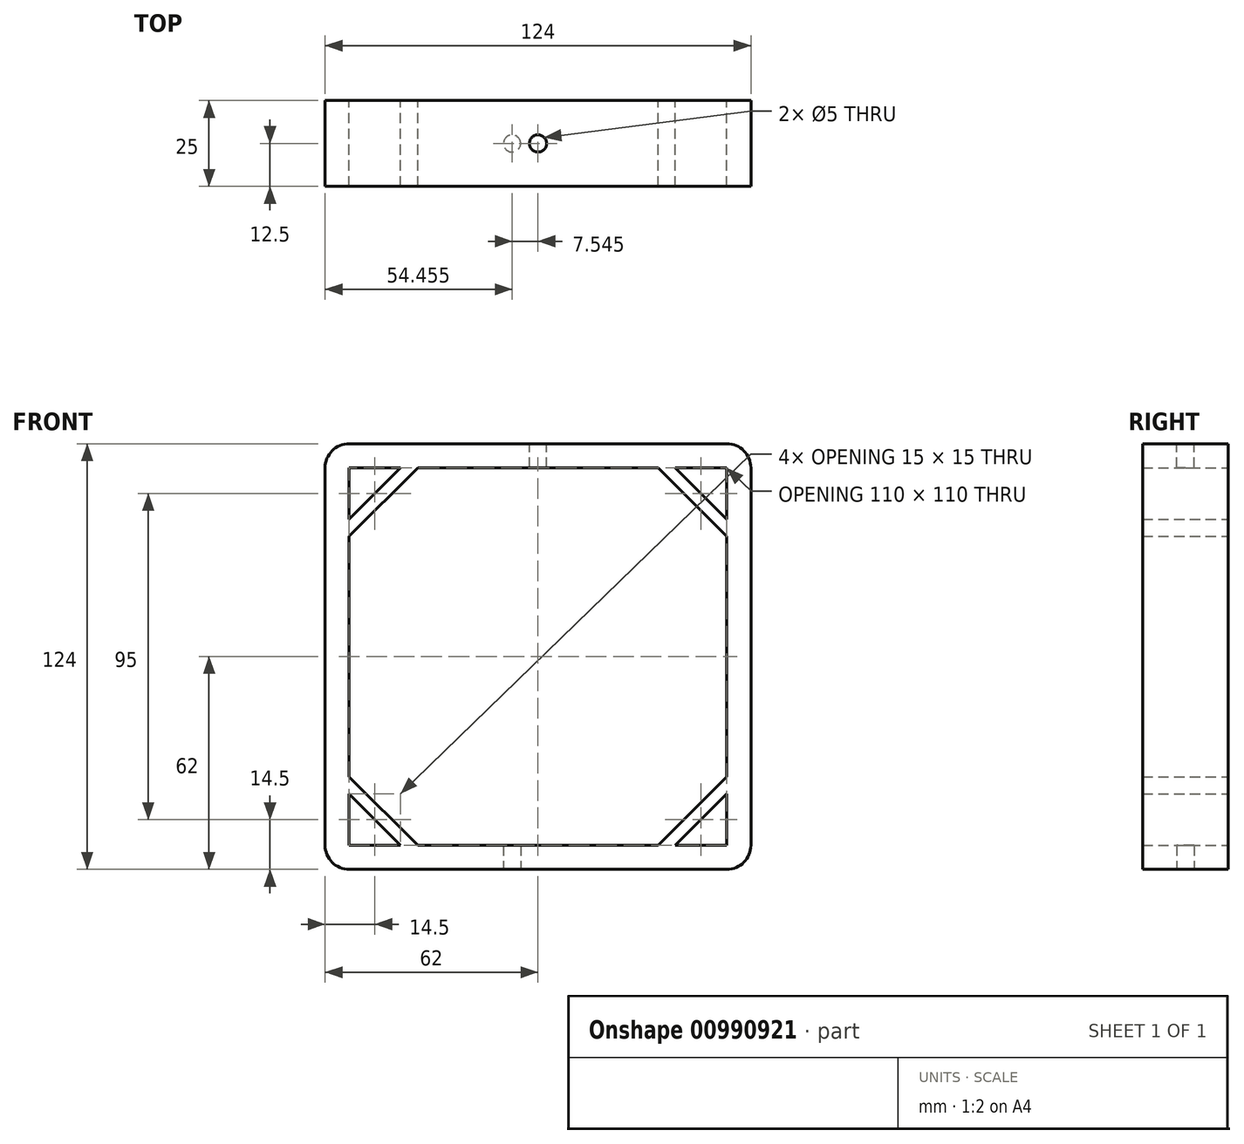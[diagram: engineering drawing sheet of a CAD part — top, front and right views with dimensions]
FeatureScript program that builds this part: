
annotation { "Feature Type Name" : "Feature", "Feature Type Description" : "" }
export const myFeature = defineFeature(function(context is Context, id is Id, definition is map)
    precondition{}
    {
        {
            var Q0;
            Q0=qCreatedBy(makeId("Front.planeOp"),FACE);
            var sketch = newSketch(context, id + "F0", { "sketchPlane" : qUnion([Q0])});
            skLineSegment(sketch, "E0.bottom", {"start": v(55, 55) * mm, "end": v(-55, 55) * mm});
            skLineSegment(sketch, "E0.top", {"start": v(55, 62) * mm, "end": v(-55, 62) * mm});
            skLineSegment(sketch, "E0.left", {"start": v(55, 55) * mm, "end": v(55, 62) * mm});
            skLineSegment(sketch, "E0.right", {"start": v(-55, 55) * mm, "end": v(-55, 62) * mm, "construction": true});
            skPoint(sketch, "E0.middle", {"position": v(0, 58.5) * mm});
            skLineSegment(sketch, "E1.MirrorCS", {"start": v(-55, -55) * mm, "end": v(-55, -62) * mm});
            skLineSegment(sketch, "E2.MirrorCS", {"start": v(55, -62) * mm, "end": v(-55, -62) * mm});
            skLineSegment(sketch, "E3.MirrorCS", {"start": v(55, -55) * mm, "end": v(55, -62) * mm, "construction": true});
            skLineSegment(sketch, "E4.MirrorCS", {"start": v(55, -55) * mm, "end": v(-55, -55) * mm});
            skArc(sketch, "E5", {"start": v(62, -55) * mm, "mid": v(59.95, -59.95) * mm, "end": v(55, -62) * mm});
            skArc(sketch, "E6", {"start": v(-62, 55) * mm, "mid": v(-59.95, 59.95) * mm, "end": v(-55, 62) * mm});
            skArc(sketch, "E7", {"start": v(55, 62) * mm, "mid": v(59.95, 59.95) * mm, "end": v(62, 55) * mm});
            skArc(sketch, "E8", {"start": v(-55, -62) * mm, "mid": v(-59.95, -59.95) * mm, "end": v(-62, -55) * mm});
            skLineSegment(sketch, "E9", {"start": v(-55, 55) * mm, "end": v(-55, -55) * mm});
            skLineSegment(sketch, "E10", {"start": v(-62, 55) * mm, "end": v(-62, -55) * mm});
            skLineSegment(sketch, "E11", {"start": v(55, 55) * mm, "end": v(55, -55) * mm});
            skLineSegment(sketch, "E12", {"start": v(62, 55) * mm, "end": v(62, -55) * mm});
            skPoint(sketch, "E13", {"position": v(-55, 40) * mm});
            skPoint(sketch, "E14", {"position": v(-55, 35) * mm});
            skPoint(sketch, "E15.MirrorP", {"position": v(55, 40) * mm});
            skPoint(sketch, "E16.MirrorP", {"position": v(55, 35) * mm});
            skPoint(sketch, "E17.MirrorP", {"position": v(-55, -35) * mm});
            skPoint(sketch, "E18.MirrorP", {"position": v(-55, -40) * mm});
            skPoint(sketch, "E19.MirrorP", {"position": v(55, -35) * mm});
            skPoint(sketch, "E20.MirrorP", {"position": v(55, -40) * mm});
            skPoint(sketch, "E21.MirrorP", {"position": v(40, 55) * mm});
            skPoint(sketch, "E22.MirrorP", {"position": v(35, 55) * mm});
            skPoint(sketch, "E23.MirrorP", {"position": v(-40, -55) * mm});
            skPoint(sketch, "E24.MirrorP", {"position": v(-35, -55) * mm});
            skPoint(sketch, "E25.MirrorP", {"position": v(-40, 55) * mm});
            skPoint(sketch, "E26.MirrorP", {"position": v(-35, 55) * mm});
            skPoint(sketch, "E27.MirrorP", {"position": v(40, -55) * mm});
            skPoint(sketch, "E28.MirrorP", {"position": v(35, -55) * mm});
            skLineSegment(sketch, "E29", {"start": v(-55, 40) * mm, "end": v(-40, 55) * mm});
            skLineSegment(sketch, "E30", {"start": v(-35, 55) * mm, "end": v(-55, 35) * mm});
            skLineSegment(sketch, "E31", {"start": v(40, 55) * mm, "end": v(55, 40) * mm});
            skLineSegment(sketch, "E32", {"start": v(55, 35) * mm, "end": v(35, 55) * mm});
            skLineSegment(sketch, "E33", {"start": v(55, -40) * mm, "end": v(40, -55) * mm});
            skLineSegment(sketch, "E34", {"start": v(35, -55) * mm, "end": v(55, -35) * mm});
            skLineSegment(sketch, "E35", {"start": v(-55, -40) * mm, "end": v(-40, -55) * mm});
            skLineSegment(sketch, "E36", {"start": v(-35, -55) * mm, "end": v(-55, -35) * mm});
            skSolve(sketch);
        }
        {
            var Q0;
            Q0 = qSketchRegion(id + "F0", true);
            var Q1;
            {var subQ0=sQuery(id+"F0.wireOp",EDGE,"E29");Q1=makeQuery(id+"F0.imprint","IMPRINT",FACE,{"disambiguationData":[TD([[makeQuery(id+"F0.imprint","IMPRINT",EDGE,{"derivedFrom":subQ0}),-1.0]])]});}
            var Q2;
            {var subQ2=sQuery(id+"F0.wireOp",EDGE,"E31");Q2=makeQuery(id+"F0.imprint","IMPRINT",FACE,{"disambiguationData":[TD([[makeQuery(id+"F0.imprint","IMPRINT",EDGE,{"derivedFrom":subQ2}),-1.0]])]});}
            var Q3;
            {var subQ2=sQuery(id+"F0.wireOp",EDGE,"E33");Q3=makeQuery(id+"F0.imprint","IMPRINT",FACE,{"disambiguationData":[TD([[makeQuery(id+"F0.imprint","IMPRINT",EDGE,{"derivedFrom":subQ2}),-1.0]])]});}
            var Q4;
            {var subQ0=sQuery(id+"F0.wireOp",EDGE,"E35");Q4=makeQuery(id+"F0.imprint","IMPRINT",FACE,{"disambiguationData":[TD([[makeQuery(id+"F0.imprint","IMPRINT",EDGE,{"derivedFrom":subQ0}),1.0]])]});}
            extrude(context, id + "F1", {"entities" : qUnion([Q0, Q1, Q2, Q3, Q4]), "depth" : 25 * mm, "offsetDistance" : 25 * mm});
        }
        {
            var Q0;
            Q0=makeQuery(id+"F1.opExtrude","SWEPT_FACE",FACE,{"disambiguationData":[OSD([sQuery(id+"F0.wireOp",EDGE,"E0.top")])]});
            var sketch = newSketch(context, id + "F2", { "sketchPlane" : qUnion([Q0])});
            skPoint(sketch, "E37", {"position": v(-55, -12.5) * mm});
            skLineSegment(sketch, "E38", {"start": v(-55, -12.5) * mm, "end": v(55, -12.5) * mm, "construction": true});
            skCircle(sketch, "E39", {"center": v(0, -12.5) * mm, "radius": 2.5 * mm});
            skSolve(sketch);
        }
        {
            var Q0;
            Q0=makeQuery(id+"F1.opExtrude","SWEPT_FACE",FACE,{"disambiguationData":[OSD([sQuery(id+"F0.wireOp",EDGE,"E2.MirrorCS")])]});
            var sketch = newSketch(context, id + "F3", { "sketchPlane" : qUnion([Q0])});
            skLineSegment(sketch, "E40", {"start": v(-55, 12.5) * mm, "end": v(39.9, 12.5) * mm, "construction": true});
            skCircle(sketch, "E41", {"center": v(-7.55, 12.5) * mm, "radius": 2.5 * mm});
            skSolve(sketch);
        }
        {
            var Q0;
            Q0=makeQuery(id+"F3.imprint","IMPRINT",FACE,{"disambiguationData":[TD([[makeQuery(id+"F3.imprint","IMPRINT",EDGE,{"derivedFrom":sQuery(id+"F3.wireOp",EDGE,"E41")}),1.0]])]});
            extrude(context, id + "F4", {"entities" : qUnion([Q0]), "operationType" : NewBodyOperationType.REMOVE, "oppositeDirection" : true, "depth" : 25 * mm, "offsetDistance" : 25 * mm});
        }
        {
            var Q0;
            Q0=makeQuery(id+"F2.imprint","IMPRINT",FACE,{"disambiguationData":[TD([[makeQuery(id+"F2.imprint","IMPRINT",EDGE,{"derivedFrom":sQuery(id+"F2.wireOp",EDGE,"E39")}),1.0]])]});
            extrude(context, id + "F5", {"entities" : qUnion([Q0]), "operationType" : NewBodyOperationType.REMOVE, "oppositeDirection" : true, "depth" : 25 * mm, "offsetDistance" : 25 * mm});
        }
    });
